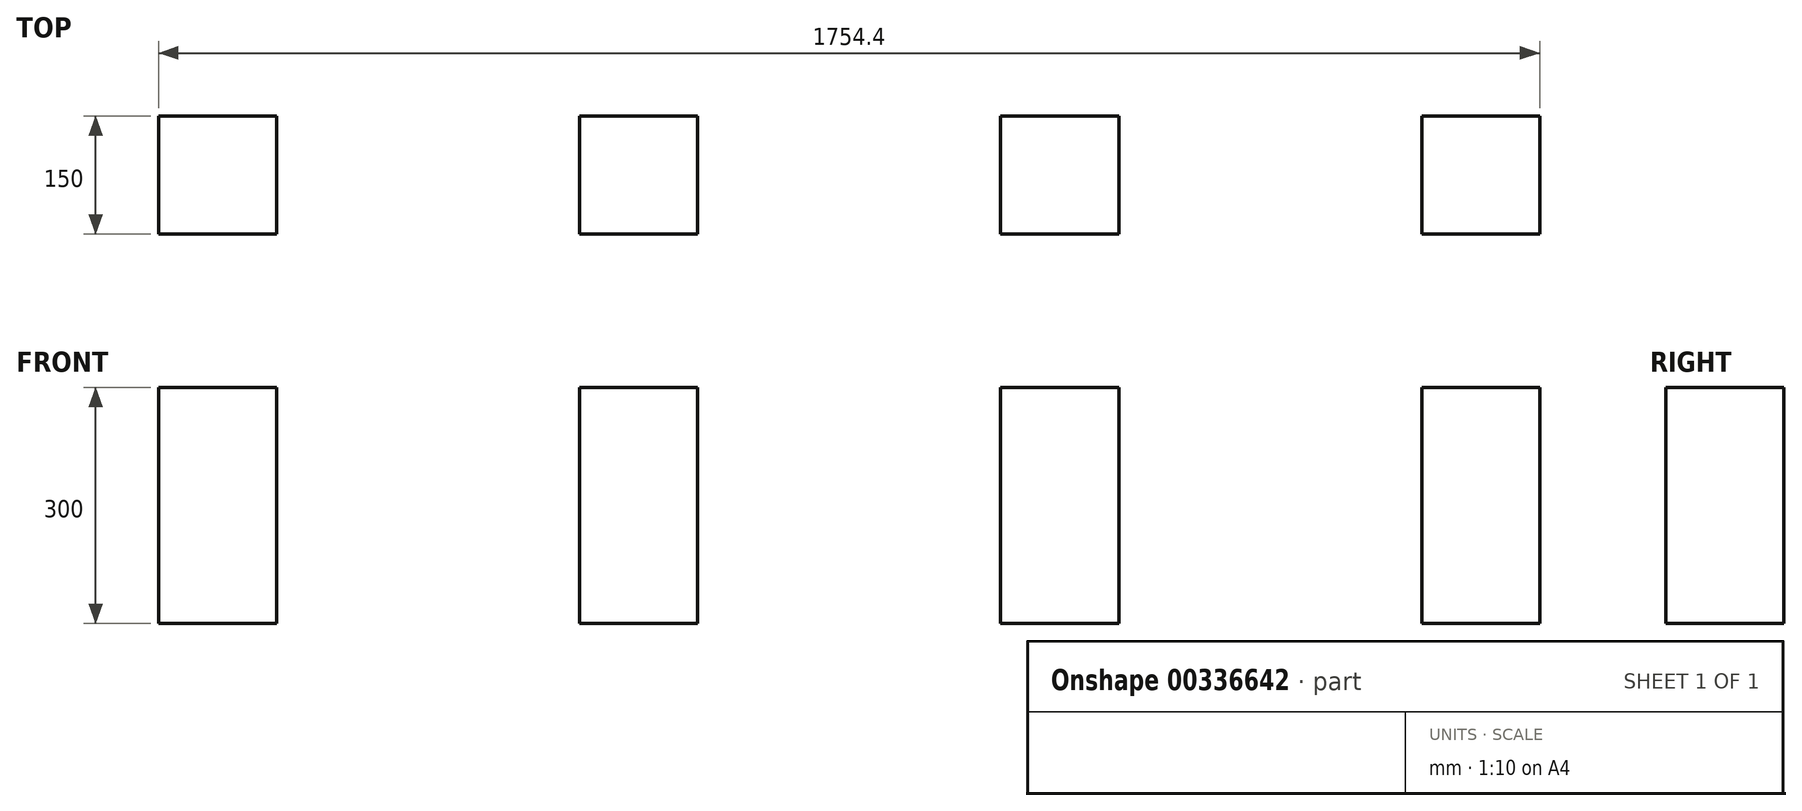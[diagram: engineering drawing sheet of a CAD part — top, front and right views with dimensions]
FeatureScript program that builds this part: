
annotation { "Feature Type Name" : "Feature", "Feature Type Description" : "" }
export const myFeature = defineFeature(function(context is Context, id is Id, definition is map)
    precondition{}
    {
        {
            var Q0;
            Q0=qCreatedBy(makeId("Top.planeOp"),FACE);
            var sketch = newSketch(context, id + "F0", { "sketchPlane" : qUnion([Q0])});
            skLineSegment(sketch, "E0.bottom", {"start": v(-1318.3, 150) * mm, "end": v(-1168.3, 150) * mm});
            skLineSegment(sketch, "E0.top", {"start": v(-1318.3, 0) * mm, "end": v(-1168.3, 0) * mm});
            skLineSegment(sketch, "E0.left", {"start": v(-1318.3, 150) * mm, "end": v(-1318.3, 0) * mm});
            skLineSegment(sketch, "E0.right", {"start": v(-1168.3, 150) * mm, "end": v(-1168.3, 0) * mm});
            skLineSegment(sketch, "E1.bottom", {"start": v(-783.5, 150) * mm, "end": v(-633.5, 150) * mm});
            skLineSegment(sketch, "E1.top", {"start": v(-783.5, 0) * mm, "end": v(-633.5, 0) * mm});
            skLineSegment(sketch, "E1.left", {"start": v(-783.5, 150) * mm, "end": v(-783.5, 0) * mm});
            skLineSegment(sketch, "E1.right", {"start": v(-633.5, 150) * mm, "end": v(-633.5, 0) * mm});
            skLineSegment(sketch, "E2.bottom", {"start": v(-248.7, 150) * mm, "end": v(-98.7, 150) * mm});
            skLineSegment(sketch, "E2.top", {"start": v(-248.7, 0) * mm, "end": v(-98.7, 0) * mm});
            skLineSegment(sketch, "E2.left", {"start": v(-248.7, 150) * mm, "end": v(-248.7, 0) * mm});
            skLineSegment(sketch, "E2.right", {"start": v(-98.7, 150) * mm, "end": v(-98.7, 0) * mm});
            skLineSegment(sketch, "E3.bottom", {"start": v(286.1, 150) * mm, "end": v(436.1, 150) * mm});
            skLineSegment(sketch, "E3.top", {"start": v(286.1, 0) * mm, "end": v(436.1, 0) * mm});
            skLineSegment(sketch, "E3.left", {"start": v(286.1, 150) * mm, "end": v(286.1, 0) * mm});
            skLineSegment(sketch, "E3.right", {"start": v(436.1, 150) * mm, "end": v(436.1, 0) * mm});
            skSolve(sketch);
        }
        {
            var Q0;
            Q0 = qSketchRegion(id + "F0", true);
            extrude(context, id + "F1", {"entities" : qUnion([Q0]), "depth" : 300 * mm});
        }
    });
